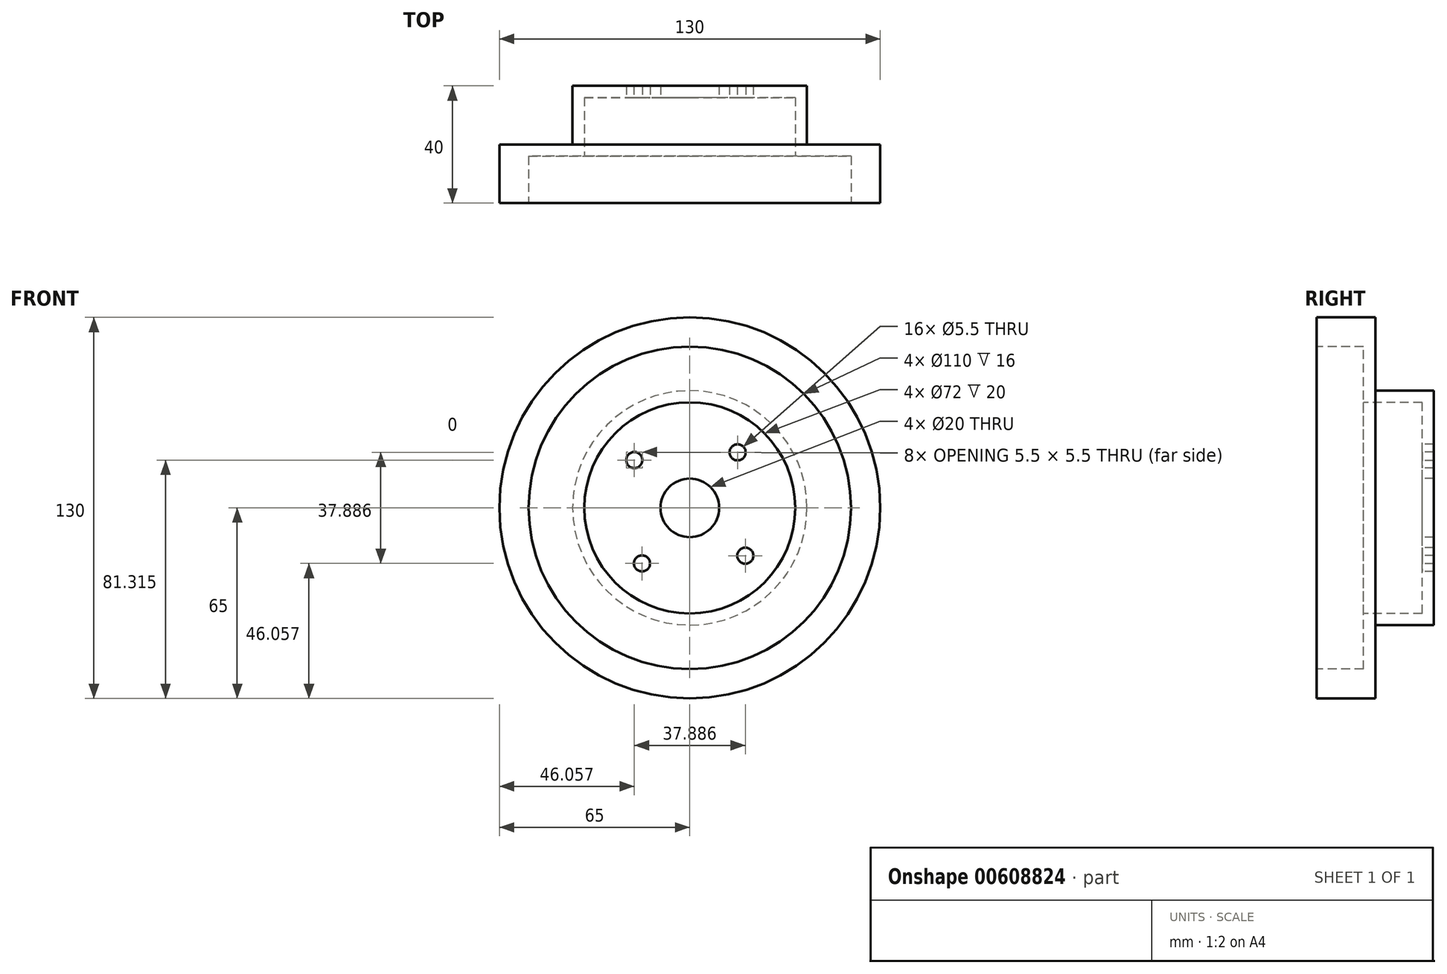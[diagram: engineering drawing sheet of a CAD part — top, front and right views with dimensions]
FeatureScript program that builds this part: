
annotation { "Feature Type Name" : "Feature", "Feature Type Description" : "" }
export const myFeature = defineFeature(function(context is Context, id is Id, definition is map)
    precondition{}
    {
        {
            var Q0;
            Q0=qCreatedBy(makeId("Right.planeOp"),FACE);
            var sketch = newSketch(context, id + "F0", { "sketchPlane" : qUnion([Q0])});
            skLineSegment(sketch, "E0", {"start": v(0, 55) * mm, "end": v(0, 65) * mm});
            skLineSegment(sketch, "E1", {"start": v(0, 65) * mm, "end": v(20, 65) * mm});
            skLineSegment(sketch, "E2", {"start": v(20, 65) * mm, "end": v(20, 40) * mm});
            skLineSegment(sketch, "E3", {"start": v(20, 40) * mm, "end": v(40, 40) * mm});
            skLineSegment(sketch, "E4", {"start": v(40, 40) * mm, "end": v(40, 10) * mm});
            skLineSegment(sketch, "E5", {"start": v(40, 10) * mm, "end": v(36, 10) * mm});
            skLineSegment(sketch, "E6", {"start": v(36, 10) * mm, "end": v(36, 36) * mm});
            skLineSegment(sketch, "E7", {"start": v(36, 36) * mm, "end": v(16, 36) * mm});
            skLineSegment(sketch, "E8", {"start": v(16, 36) * mm, "end": v(16, 55) * mm});
            skLineSegment(sketch, "E9", {"start": v(16, 55) * mm, "end": v(0, 55) * mm});
            skLineSegment(sketch, "E10", {"start": v(0, 0) * mm, "end": v(75.53, 0) * mm});
            skSolve(sketch);
        }
        {
            var Q0;
            Q0 = qSketchRegion(id + "F0", true);
            var Q1;
            Q1=sQuery(id+"F0.wireOp",EDGE,"E10");
            revolve(context, id + "F1", {"entities" : qUnion([Q0]), "axis" : qUnion([Q1]), "revolveType" : RevolveType.FULL});
        }
        {
            var Q0;
            Q0=makeQuery(id+"F1.opRevolve","SWEPT_FACE",FACE,{"disambiguationData":[OSD([sQuery(id+"F0.wireOp",EDGE,"E6")])]});
            var sketch = newSketch(context, id + "F2", { "sketchPlane" : qUnion([Q0])});
            skCircle(sketch, "E11", {"center": v(0, 0) * mm, "radius": 25 * mm, "construction": true});
            skCircle(sketch, "E12", {"center": v(16.31, 18.94) * mm, "radius": 2.75 * mm});
            skSolve(sketch);
        }
        {
            var Q0;
            Q0 = qSketchRegion(id + "F2", true);
            extrude(context, id + "F3", {"entities" : qUnion([Q0]), "endBound" : BoundingType.UP_TO_NEXT, "oppositeDirection" : true, "depth" : 25 * mm, "offsetDistance" : 25 * mm});
        }
        {
            var Q0;
            Q0=qCreatedBy(makeId("Right.planeOp"),FACE);
            var sketch = newSketch(context, id + "F4", { "sketchPlane" : qUnion([Q0])});
            skLineSegment(sketch, "E13", {"start": v(0, 0) * mm, "end": v(90.13, 0) * mm});
            skSolve(sketch);
        }
        {
            var Q0;
            Q0=makeQuery(id+"F3.opExtrude","SWEPT_BODY",BODY,{"disambiguationData":[OSD([sQuery(id+"F2.wireOp",EDGE,"E12")])]});
            var Q1;
            Q1=sQuery(id+"F4.wireOp",EDGE,"E13");
            var Q2;
            Q2=makeQuery(id+"F1.opRevolve","SWEPT_BODY",BODY,{"disambiguationData":[OSD([sQuery(id+"F0.wireOp",EDGE,"E0"),sQuery(id+"F0.wireOp",EDGE,"E1"),sQuery(id+"F0.wireOp",EDGE,"E2"),sQuery(id+"F0.wireOp",EDGE,"E3"),sQuery(id+"F0.wireOp",EDGE,"E4"),sQuery(id+"F0.wireOp",EDGE,"E5"),sQuery(id+"F0.wireOp",EDGE,"E6"),sQuery(id+"F0.wireOp",EDGE,"E7"),sQuery(id+"F0.wireOp",EDGE,"E8"),sQuery(id+"F0.wireOp",EDGE,"E9")])]});
            circularPattern(context, id + "F5", {"operationType" : NewBodyOperationType.REMOVE, "entities" : qUnion([Q0]), "axis" : qUnion([Q1]), "angle" : 360 * degree, "instanceCount" : 4, "equalSpace" : true});
        }
    });
